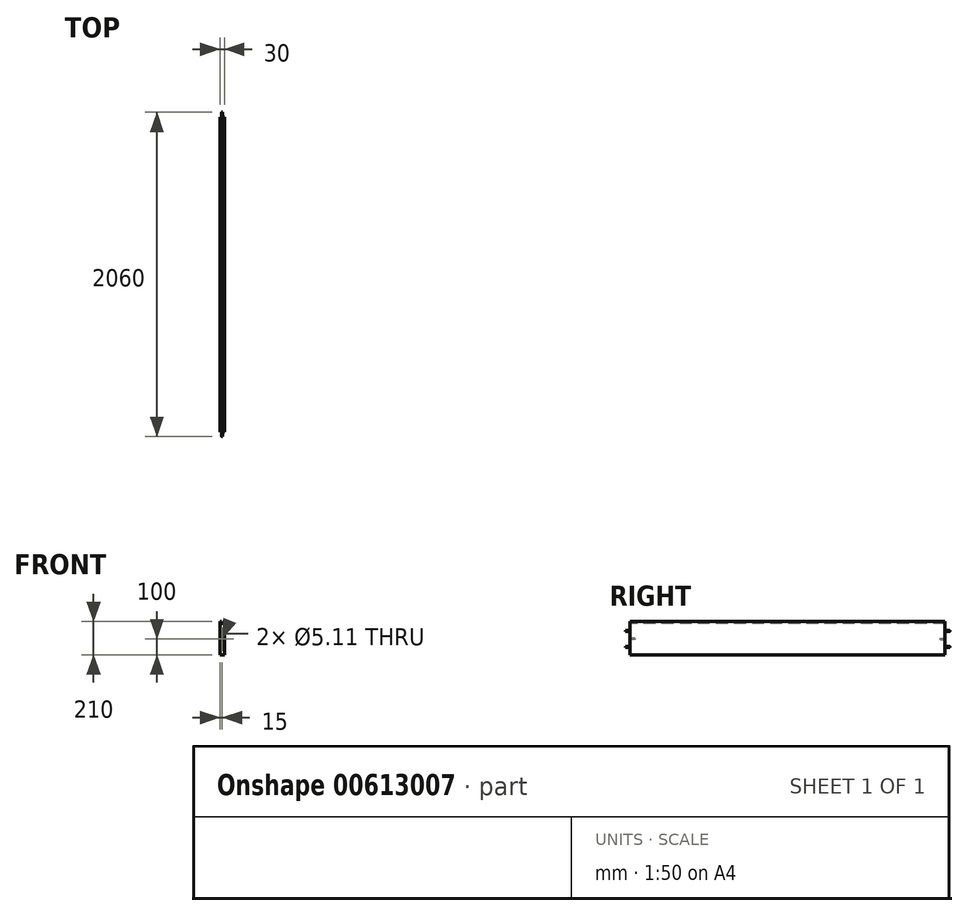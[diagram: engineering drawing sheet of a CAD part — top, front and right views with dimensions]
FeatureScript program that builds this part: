
annotation { "Feature Type Name" : "Feature", "Feature Type Description" : "" }
export const myFeature = defineFeature(function(context is Context, id is Id, definition is map)
    precondition{}
    {
        {
            var Q0;
            Q0=qCreatedBy(makeId("Right.planeOp"),FACE);
            var sketch = newSketch(context, id + "F0", { "sketchPlane" : qUnion([Q0])});
            skLineSegment(sketch, "E0.bottom", {"start": v(1000, -100) * mm, "end": v(-1000, -100) * mm});
            skLineSegment(sketch, "E0.top", {"start": v(1000, 100) * mm, "end": v(-1000, 100) * mm});
            skLineSegment(sketch, "E0.left", {"start": v(1000, -100) * mm, "end": v(1000, 100) * mm});
            skLineSegment(sketch, "E0.right", {"start": v(-1000, -100) * mm, "end": v(-1000, 100) * mm});
            skPoint(sketch, "E0.middle", {"position": v(0, 0) * mm});
            skSolve(sketch);
        }
        {
            var Q0;
            Q0=qSketchRegion(id+"F0",true);
            extrude(context, id + "F1", {"entities" : qUnion([Q0]), "depth" : 30 * mm, "offsetDistance" : 25 * mm});
        }
        {
            var Q0;
            Q0=makeQuery(id+"F1.opExtrude","SWEPT_FACE",FACE,{"disambiguationData":[OSD([sQuery(id+"F0.wireOp",EDGE,"E0.right")])]});
            var sketch = newSketch(context, id + "F2", { "sketchPlane" : qUnion([Q0])});
            skLineSegment(sketch, "E1.bottom", {"start": v(10, 100) * mm, "end": v(0, 100) * mm});
            skLineSegment(sketch, "E1.top", {"start": v(10, 110) * mm, "end": v(0, 110) * mm});
            skLineSegment(sketch, "E1.left", {"start": v(10, 100) * mm, "end": v(10, 110) * mm});
            skLineSegment(sketch, "E1.right", {"start": v(0, 100) * mm, "end": v(0, 110) * mm});
            skPoint(sketch, "E1.middle", {"position": v(5, 105) * mm});
            skSolve(sketch);
        }
        {
            var Q0;
            Q0=qSketchRegion(id+"F2",true);
            extrude(context, id + "F3", {"entities" : qUnion([Q0]), "operationType" : NewBodyOperationType.ADD, "depth" : -2000 * mm, "offsetDistance" : 25 * mm});
        }
        {
            var Q0;
            Q0=makeQuery(id+"F3.boolean.opBoolean","MERGE",FACE,{"derivedFrom":[makeQuery(id+"F1.opExtrude","SWEPT_FACE",FACE,{"disambiguationData":[OSD([sQuery(id+"F0.wireOp",EDGE,"E0.right")])]}),makeQuery(id+"F3.opExtrude","CAP_FACE",FACE,{"disambiguationData":[OSD([sQuery(id+"F2.wireOp",EDGE,"E1.bottom"),sQuery(id+"F2.wireOp",EDGE,"E1.top"),sQuery(id+"F2.wireOp",EDGE,"E1.left"),sQuery(id+"F2.wireOp",EDGE,"E1.right")])],"isStart":true})]});
            var sketch = newSketch(context, id + "F4", { "sketchPlane" : qUnion([Q0])});
            skLineSegment(sketch, "E2.bottom", {"start": v(30, 100) * mm, "end": v(20, 100) * mm});
            skLineSegment(sketch, "E2.top", {"start": v(30, 110) * mm, "end": v(20, 110) * mm});
            skLineSegment(sketch, "E2.left", {"start": v(30, 100) * mm, "end": v(30, 110) * mm});
            skLineSegment(sketch, "E2.right", {"start": v(20, 100) * mm, "end": v(20, 110) * mm});
            skPoint(sketch, "E2.middle", {"position": v(25, 105) * mm});
            skSolve(sketch);
        }
        {
            var Q0;
            Q0=makeQuery(id+"FdNdVz6oqzI9myz_1.boolean.opBoolean","MERGE",FACE,{"derivedFrom":[makeQuery(id+"F3.boolean.opBoolean","MERGE",FACE,{"derivedFrom":[makeQuery(id+"F1.opExtrude","SWEPT_FACE",FACE,{"disambiguationData":[OSD([sQuery(id+"F0.wireOp",EDGE,"E0.left")])]}),makeQuery(id+"F3.opExtrude","CAP_FACE",FACE,{"disambiguationData":[OSD([sQuery(id+"F2.wireOp",EDGE,"E1.bottom"),sQuery(id+"F2.wireOp",EDGE,"E1.top"),sQuery(id+"F2.wireOp",EDGE,"E1.left"),sQuery(id+"F2.wireOp",EDGE,"E1.right")])],"isStart":false})]}),makeQuery(id+"FdNdVz6oqzI9myz_1.opExtrude","CAP_FACE",FACE,{"disambiguationData":[OSD([sQuery(id+"F4.wireOp",EDGE,"E2.bottom"),sQuery(id+"F4.wireOp",EDGE,"E2.top"),sQuery(id+"F4.wireOp",EDGE,"E2.left"),sQuery(id+"F4.wireOp",EDGE,"E2.right")])],"isStart":false})]});
            var sketch = newSketch(context, id + "F5", { "sketchPlane" : qUnion([Q0])});
            skCircle(sketch, "E3", {"center": v(-15, 50.25) * mm, "radius": 3 * mm});
            skCircle(sketch, "E4", {"center": v(-15, -50) * mm, "radius": 3 * mm});
            skSolve(sketch);
        }
        {
            var Q0;
            Q0=makeQuery(id+"F5.imprint","IMPRINT",FACE,{"disambiguationData":[TD([[makeQuery(id+"F5.imprint","IMPRINT",EDGE,{"derivedFrom":sQuery(id+"F5.wireOp",EDGE,"E4")}),1.0]])]});
            var Q1;
            Q1=makeQuery(id+"F5.imprint","IMPRINT",FACE,{"disambiguationData":[TD([[makeQuery(id+"F5.imprint","IMPRINT",EDGE,{"derivedFrom":sQuery(id+"F5.wireOp",EDGE,"E3")}),1.0]])]});
            extrude(context, id + "F6", {"entities" : qUnion([Q0, Q1]), "operationType" : NewBodyOperationType.ADD, "depth" : 30 * mm, "offsetDistance" : 25 * mm});
        }
        {
            var Q0;
            {var subQ1=sQuery(id+"F4.wireOp",EDGE,"E2.bottom");Q0=makeQuery(id+"F4.imprint","IMPRINT",FACE,{"disambiguationData":[TD([[makeQuery(id+"F4.imprint","IMPRINT",EDGE,{"derivedFrom":subQ1}),1.0]])]});}
            var sketch = newSketch(context, id + "F7", { "sketchPlane" : qUnion([Q0])});
            skCircle(sketch, "E5", {"center": v(15, 50) * mm, "radius": 3 * mm});
            skCircle(sketch, "E6", {"center": v(15, -50) * mm, "radius": 3 * mm});
            skSolve(sketch);
        }
        {
            var Q0;
            Q0=makeQuery(id+"F7.imprint","IMPRINT",FACE,{"disambiguationData":[TD([[makeQuery(id+"F7.imprint","IMPRINT",EDGE,{"derivedFrom":sQuery(id+"F7.wireOp",EDGE,"E5")}),1.0]])]});
            var Q1;
            Q1=makeQuery(id+"F7.imprint","IMPRINT",FACE,{"disambiguationData":[TD([[makeQuery(id+"F7.imprint","IMPRINT",EDGE,{"derivedFrom":sQuery(id+"F7.wireOp",EDGE,"E6")}),1.0]])]});
            extrude(context, id + "F8", {"entities" : qUnion([Q0, Q1]), "operationType" : NewBodyOperationType.ADD, "depth" : 30 * mm, "offsetDistance" : 25 * mm});
        }
        {
            var Q0;
            Q0 = qSketchRegion(id + "F4", true);
            extrude(context, id + "F9", {"entities" : qUnion([Q0]), "operationType" : NewBodyOperationType.ADD, "depth" : -2000 * mm, "offsetDistance" : 25 * mm});
        }
        {
            var Q0;
            Q0=makeQuery(id+"F7.imprint","IMPRINT",FACE,{"disambiguationData":[TD([[makeQuery(id+"F7.imprint","IMPRINT",EDGE,{"derivedFrom":sQuery(id+"F7.wireOp",EDGE,"E5")}),-1.0]])]});
            var sketch = newSketch(context, id + "F10", { "sketchPlane" : qUnion([Q0])});
            skCircle(sketch, "E7", {"center": v(15, 0) * mm, "radius": 3 * mm});
            skSolve(sketch);
        }
        {
            var Q0;
            Q0=sQuery(id+"F10.wireOp",VERTEX,"E7.center");
            var Q1;
            Q1=makeQuery(id+"F1.opExtrude","SWEPT_BODY",BODY,{"disambiguationData":[OSD([sQuery(id+"F0.wireOp",EDGE,"E0.bottom"),sQuery(id+"F0.wireOp",EDGE,"E0.top"),sQuery(id+"F0.wireOp",EDGE,"E0.left"),sQuery(id+"F0.wireOp",EDGE,"E0.right")])]});
            hole(context, id + "F11", {"style" : HoleStyle.SIMPLE, "endStyle" : HoleEndStyle.BLIND, "standardTappedOrClearance" : lookupTablePath({ "standard" : "ANSI", "engagement" : "75%", "pitch" : "20 tpi", "size" : "1/4", "type" : "Tapped" }), "standardBlindInLast" : lookupTablePath({ "standard" : "ANSI", "engagement" : "75%", "pitch" : "20 tpi", "size" : "1/4", "type" : "Tapped" }), "holeDiameter" : 5.1 * mm, "majorDiameter" : 6.35 * mm, "showTappedDepth" : true, "holeDepth" : 30 * mm, "isTappedThrough" : true, "tappedDepth" : 26.2 * mm, "tapClearance" : 3, "locations" : qUnion([Q0]), "scope" : qUnion([Q1])});
        }
        {
            var Q0;
            Q0=makeQuery(id+"F9.boolean.opBoolean","MERGE",FACE,{"derivedFrom":[makeQuery(id+"F3.boolean.opBoolean","MERGE",FACE,{"derivedFrom":[makeQuery(id+"F1.opExtrude","SWEPT_FACE",FACE,{"disambiguationData":[OSD([sQuery(id+"F0.wireOp",EDGE,"E0.left")])]}),makeQuery(id+"F3.opExtrude","CAP_FACE",FACE,{"disambiguationData":[OSD([sQuery(id+"F2.wireOp",EDGE,"E1.bottom"),sQuery(id+"F2.wireOp",EDGE,"E1.top"),sQuery(id+"F2.wireOp",EDGE,"E1.left"),sQuery(id+"F2.wireOp",EDGE,"E1.right")])],"isStart":false})]}),makeQuery(id+"F9.opExtrude","CAP_FACE",FACE,{"disambiguationData":[OSD([sQuery(id+"F4.wireOp",EDGE,"E2.bottom"),sQuery(id+"F4.wireOp",EDGE,"E2.top"),sQuery(id+"F4.wireOp",EDGE,"E2.left"),sQuery(id+"F4.wireOp",EDGE,"E2.right")])],"isStart":false})]});
            var sketch = newSketch(context, id + "F12", { "sketchPlane" : qUnion([Q0])});
            skCircle(sketch, "E8", {"center": v(-15, 0) * mm, "radius": 3 * mm});
            skSolve(sketch);
        }
        {
            var Q0;
            Q0=sQuery(id+"F12.wireOp",VERTEX,"E8.center");
            var Q1;
            Q1=makeQuery(id+"F1.opExtrude","SWEPT_BODY",BODY,{"disambiguationData":[OSD([sQuery(id+"F0.wireOp",EDGE,"E0.bottom"),sQuery(id+"F0.wireOp",EDGE,"E0.top"),sQuery(id+"F0.wireOp",EDGE,"E0.left"),sQuery(id+"F0.wireOp",EDGE,"E0.right")])]});
            hole(context, id + "F13", {"style" : HoleStyle.SIMPLE, "endStyle" : HoleEndStyle.BLIND, "standardTappedOrClearance" : lookupTablePath({ "standard" : "ANSI", "engagement" : "75%", "pitch" : "20 tpi", "size" : "1/4", "type" : "Tapped" }), "standardBlindInLast" : lookupTablePath({ "standard" : "ANSI", "engagement" : "75%", "pitch" : "20 tpi", "size" : "1/4", "type" : "Tapped" }), "holeDiameter" : 5.1 * mm, "majorDiameter" : 6.35 * mm, "showTappedDepth" : true, "holeDepth" : 30 * mm, "isTappedThrough" : true, "tappedDepth" : 26.2 * mm, "tapClearance" : 3, "locations" : qUnion([Q0]), "scope" : qUnion([Q1])});
        }
    });
